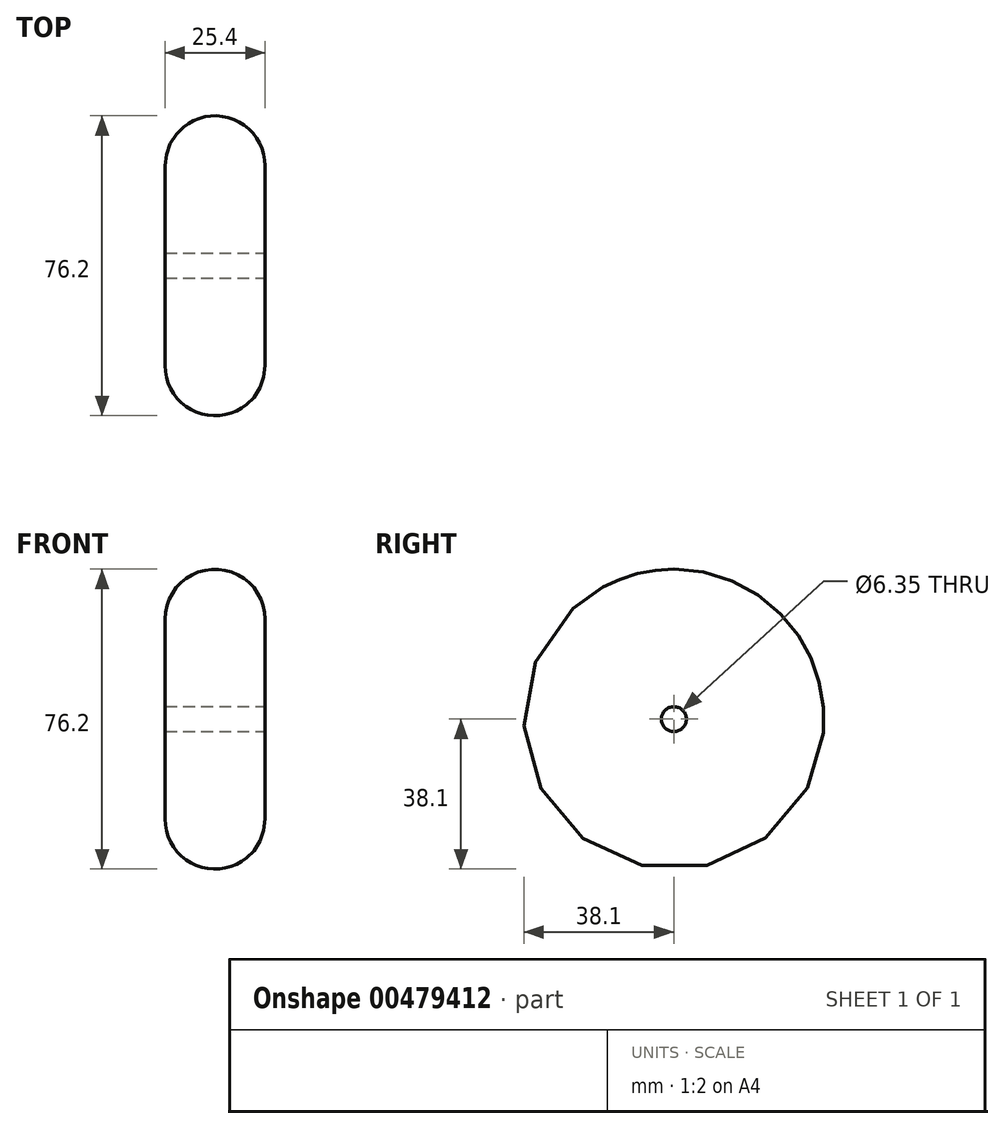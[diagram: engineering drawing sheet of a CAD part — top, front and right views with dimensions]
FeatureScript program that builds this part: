
annotation { "Feature Type Name" : "Feature", "Feature Type Description" : "" }
export const myFeature = defineFeature(function(context is Context, id is Id, definition is map)
    precondition{}
    {
        {
            var Q0;
            Q0=qCreatedBy(makeId("Top.planeOp"),FACE);
            var sketch = newSketch(context, id + "F0", { "sketchPlane" : qUnion([Q0])});
            skCircle(sketch, "E0", {"center": v(0, 25.4) * mm, "radius": 12.7 * mm});
            skLineSegment(sketch, "E1", {"start": v(-30.98, 0) * mm, "end": v(35.61, 0) * mm});
            skSolve(sketch);
        }
        {
            var Q0;
            Q0 = qSketchRegion(id + "F0", true);
            var Q1;
            Q1=sQuery(id+"F0.wireOp",EDGE,"E1");
            revolve(context, id + "F1", {"surfaceOperationType" : NewSurfaceOperationType.NEW, "entities" : qUnion([Q0]), "axis" : qUnion([Q1]), "revolveType" : RevolveType.FULL});
        }
        {
            var Q0;
            Q0=qCreatedBy(makeId("Right.planeOp"),FACE);
            var sketch = newSketch(context, id + "F2", { "sketchPlane" : qUnion([Q0])});
            skCircle(sketch, "E2", {"center": v(0, 0) * mm, "radius": 25.4 * mm});
            skSolve(sketch);
        }
        {
            var Q0;
            Q0 = qSketchRegion(id + "F2", true);
            extrude(context, id + "F3", {"entities" : qUnion([Q0]), "operationType" : NewBodyOperationType.ADD, "depth" : 25.4 * mm, "offsetDistance" : 25.4 * mm, "symmetric" : true});
        }
        {
            var Q0;
            Q0=makeQuery(id+"F3.opExtrude","CAP_FACE",FACE,{"disambiguationData":[OSD([sQuery(id+"F2.wireOp",EDGE,"E2")])],"isStart":false});
            var sketch = newSketch(context, id + "F4", { "sketchPlane" : qUnion([Q0])});
            skCircle(sketch, "E3", {"center": v(0, 0) * mm, "radius": 3.18 * mm});
            skSolve(sketch);
        }
        {
            var Q0;
            Q0 = qSketchRegion(id + "F4", true);
            extrude(context, id + "F5", {"entities" : qUnion([Q0]), "operationType" : NewBodyOperationType.REMOVE, "oppositeDirection" : true, "depth" : 25.4 * mm, "offsetDistance" : 25.4 * mm});
        }
    });
